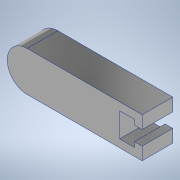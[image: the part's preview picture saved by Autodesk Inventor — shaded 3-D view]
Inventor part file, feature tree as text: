
AUTODESK INVENTOR PART (.ipt)
format: ipt  version: 2022 (Build 260153000, 153)  size: 128,512 bytes
history: native  units: mm
features: extrude x1, sketch x1
ambient origin geometry x8: Origin, YZ Plane, XZ Plane, XY Plane, X Axis, Y Axis, Z Axis, Center Point
bodies: Body1 (feature_tree)
feature tree (2):
  extrude  "Extrusion2"  Depth=9.5mm
  sketch  "Sketch5"  dims[d41=5.8mm d48=44.0mm d50=3.0mm d56=12.0mm d57=0.0mm d63=45.0mm d67=15.6mm d71=0.0mm d72=36.2mm d78=5.6mm d79=9.5mm]
